# Revit family: Hager-VECTOR-Surface_mounted-IP65-With_Cover-With_DIN-NoHosted-DE-de
name_source: partatom
category: Electrical Equipment
units: mm (PartAtom-declared; Revit-internal decimal feet)

## family parameters
Always vertical = Yes
Cut with Voids When Loaded = No
Maintain Annotation Orientation = No
Panel Configuration = Two Columns, Circuits Across
Part Type = Panelboard
Room Calculation Point = No
Round Connector Dimension = Use Diameter
Shared = No
Work Plane-Based = Yes

## types (87) — shared parameters
Code hager = ADD-EC000214_EU
Default Elevation = 1200 mm
EF000003 - Montageart = Aufputz
EF000007 - Farbe = grau
EF000024 - UV-beständig = No
EF000116 - RAL-Nummer = 7035
EF000118 - Mit Montageplatte = No
EF001062 - EMV-Ausführung = No
EF001134 - DIN-Schiene = Yes
EF004462 - Art der Schließung = sonstige
EF005474 - Schutzart (IP) = IP65
EF006306 - Mit Schloss = No
ETIM class code = EC000214
ETIM class name = Small distribution board
HG000001-Anzahl der Spalten = 1
HG000002-Mit tür = Yes
HG000003-Bereich = VECTOR
HG000005-Dicke = 2 mm  [stored 0.00656168 ft]
HG000006-Flush mounted = No
HG000009-Doppelflügeligen Tür = No
HG000010-Asymmetrische Türen = No
HG000011-Leere Reihen von unten = No
HG000012-Türschwenkwinkel = 90.00°
HG000013-Tür links = No
HG000014-Tür rechts = Yes
HG000015-Sichtbarkeit der Türöffnung = Yes
HG000016-3D-Türsichtbarkeit = Yes
HG000017-Distanz zwischen den Polen = 18 mm  [stored 0.0590551 ft]
HG000060-RAL-number = 7035
HG000099-Onfly Template ID-de-DE = 507532
Manufacturer = Hager
Name BIM&CO = Electricity
Name hager = ADD_Enclosures_EC000214
Reference = Template-Enclosure_EU-EC000214
Uniformat = Low Tension Service & Dist.
Uniformat code = D501001
zero-valued in all types: EF000218 - Einbautiefe, EF000332 - Einbauhöhe, EF000846 - Einbaubreite, EF001131 - Innentiefe, HG000007-Anzahl der leeren Spalten, HG000008-Anzahl der leeren Reihen

## per-type parameters (varying)
| type | BC_METADATA | EF000008 - Breite | EF000040 - Höhe | EF000049 - Tiefe | EF000266 - Anzahl der Reihen | EF001088 - Anbaumöglichkeit | EF002950 - Breite in Teilungseinheiten | EF006244 - Transparenter Deckel/Tür | EF009212 - Ausführung Deckel | EF015776 - Erdungsklemmenblock | EF015777 - Neutralleiterklemmenblock | EF015941 - Signaldurchlassende Tür | HG000004-Herstellerreferenz | HGEF000266-Anzahl der Reihen | HGEF0002950-Breite in Teilungseinheiten |
| VECTOR-Surface_mounted_W310_H552_D151_12_Modular_Spacing-VE312AK | {"ObjectGuid":"03e6f95a-bdcf-4ad5-8e30-8306eb141510","ModelGuid":"49ec60d2-c561-4fc0-8b60-787ba45f202c","VariantGuid":"607cdb30-8050-4ec9-9431-8f6f41ac29e4","Revision":"#11","VariantName":"VECTOR-Surface_mounted_W310_H552_D151_12_Modular_Spacing-VE312AK"} | 310 mm  [stored 1.01706 ft] | 552 mm  [stored 1.81102 ft] | 151 mm  [stored 0.495407 ft] | 3 | Yes | 12 | Yes | geschlossen | Yes | Yes | Yes | VE312AK | 3 | 12 |
| VECTOR-Surface_mounted_W310_H552_D151_36_Modular_Spacing-VE312DK | {"ObjectGuid":"03e6f95a-bdcf-4ad5-8e30-8306eb141510","ModelGuid":"49ec60d2-c561-4fc0-8b60-787ba45f202c","VariantGuid":"d6fdc3a8-bad4-40ab-905a-8434b4d1adf6","Revision":"#11","VariantName":"VECTOR-Surface_mounted_W310_H552_D151_36_Modular_Spacing-VE312DK"} | 310 mm  [stored 1.01706 ft] | 552 mm  [stored 1.81102 ft] | 151 mm  [stored 0.495407 ft] | 3 | Yes | 36 | Yes | geschlossen | No | No | Yes | VE312DK | 3 | 36 |
| VECTOR-Surface_mounted_W310_H552_D151_12_Modular_Spacing-VE312DN | {"ObjectGuid":"03e6f95a-bdcf-4ad5-8e30-8306eb141510","ModelGuid":"49ec60d2-c561-4fc0-8b60-787ba45f202c","VariantGuid":"e0a0b13a-2f78-4e79-9cb4-df8ea80ce2be","Revision":"#11","VariantName":"VECTOR-Surface_mounted_W310_H552_D151_12_Modular_Spacing-VE312DN"} | 310 mm  [stored 1.01706 ft] | 552 mm  [stored 1.81102 ft] | 151 mm  [stored 0.495407 ft] | 3 | Yes | 12 | Yes | geschlossen | Yes | Yes | Yes | VE312DN | 3 | 12 |
| VECTOR-Surface_mounted_W310_H552_D151_12_Modular_Spacing-VE312F | {"ObjectGuid":"03e6f95a-bdcf-4ad5-8e30-8306eb141510","ModelGuid":"49ec60d2-c561-4fc0-8b60-787ba45f202c","VariantGuid":"a51da385-521d-42e7-b15b-fe15b541e67b","Revision":"#11","VariantName":"VECTOR-Surface_mounted_W310_H552_D151_12_Modular_Spacing-VE312F"} | 310 mm  [stored 1.01706 ft] | 552 mm  [stored 1.81102 ft] | 151 mm  [stored 0.495407 ft] | 3 | Yes | 12 | No | geschlossen | Yes | No | Yes | VE312F | 3 | 12 |
| VECTOR-Surface_mounted_W310_H552_D151_12_Modular_Spacing-VE312L | {"ObjectGuid":"03e6f95a-bdcf-4ad5-8e30-8306eb141510","ModelGuid":"49ec60d2-c561-4fc0-8b60-787ba45f202c","VariantGuid":"6e8b8deb-b106-49c2-b92e-4b4428fcabe4","Revision":"#11","VariantName":"VECTOR-Surface_mounted_W310_H552_D151_12_Modular_Spacing-VE312L"} | 310 mm  [stored 1.01706 ft] | 552 mm  [stored 1.81102 ft] | 151 mm  [stored 0.495407 ft] | 3 | Yes | 12 | Yes | mit Ausschnitt | Yes | Yes | Yes | VE312L | 3 | 12 |
| VECTOR-Surface_mounted_W310_H552_D151_36_Modular_Spacing-VE312N | {"ObjectGuid":"03e6f95a-bdcf-4ad5-8e30-8306eb141510","ModelGuid":"49ec60d2-c561-4fc0-8b60-787ba45f202c","VariantGuid":"671be7f2-69a9-4b2d-b5fc-3d919ee885c0","Revision":"#11","VariantName":"VECTOR-Surface_mounted_W310_H552_D151_36_Modular_Spacing-VE312N"} | 310 mm  [stored 1.01706 ft] | 552 mm  [stored 1.81102 ft] | 151 mm  [stored 0.495407 ft] | 3 | Yes | 36 | Yes | geschlossen | Yes | Yes | Yes | VE312N | 3 | 36 |
| VECTOR-Surface_mounted_W310_H552_D151_12_Modular_Spacing-VE312PN | {"ObjectGuid":"03e6f95a-bdcf-4ad5-8e30-8306eb141510","ModelGuid":"49ec60d2-c561-4fc0-8b60-787ba45f202c","VariantGuid":"5d3d3522-fa09-46ff-862d-f1016403435b","Revision":"#11","VariantName":"VECTOR-Surface_mounted_W310_H552_D151_12_Modular_Spacing-VE312PN"} | 310 mm  [stored 1.01706 ft] | 552 mm  [stored 1.81102 ft] | 151 mm  [stored 0.495407 ft] | 3 | Yes | 12 | Yes | geschlossen | No | No | Yes | VE312PN | 3 | 12 |
| VECTOR-Surface_mounted_W310_H552_D151_12_Modular_Spacing-VE312S | {"ObjectGuid":"03e6f95a-bdcf-4ad5-8e30-8306eb141510","ModelGuid":"49ec60d2-c561-4fc0-8b60-787ba45f202c","VariantGuid":"071b8a18-1f4b-4499-85d7-62c8f9297f1b","Revision":"#11","VariantName":"VECTOR-Surface_mounted_W310_H552_D151_12_Modular_Spacing-VE312S"} | 310 mm  [stored 1.01706 ft] | 552 mm  [stored 1.81102 ft] | 151 mm  [stored 0.495407 ft] | 3 | Yes | 12 | No | geschlossen | Yes | Yes | Yes | VE312S | 3 | 12 |
| VECTOR-Surface_mounted_W310_H552_D151_12_Modular_Spacing-VE312SN | {"ObjectGuid":"03e6f95a-bdcf-4ad5-8e30-8306eb141510","ModelGuid":"49ec60d2-c561-4fc0-8b60-787ba45f202c","VariantGuid":"53cd1ff2-2b29-469f-bbba-6836d89362b1","Revision":"#11","VariantName":"VECTOR-Surface_mounted_W310_H552_D151_12_Modular_Spacing-VE312SN"} | 310 mm  [stored 1.01706 ft] | 552 mm  [stored 1.81102 ft] | 151 mm  [stored 0.495407 ft] | 3 | Yes | 12 | Yes | mit Ausschnitt | No | No | Yes | VE312SN | 3 | 12 |
| VECTOR-Surface_mounted_W418_H602_D151_18_Modular_Spacing-VE318AK | {"ObjectGuid":"03e6f95a-bdcf-4ad5-8e30-8306eb141510","ModelGuid":"49ec60d2-c561-4fc0-8b60-787ba45f202c","VariantGuid":"4236e502-4e81-4f1a-bf8d-444f96f3dce0","Revision":"#11","VariantName":"VECTOR-Surface_mounted_W418_H602_D151_18_Modular_Spacing-VE318AK"} | 418 mm  [stored 1.37139 ft] | 602 mm  [stored 1.97507 ft] | 151 mm  [stored 0.495407 ft] | 3 | Yes | 18 | Yes | geschlossen | Yes | Yes | Yes | VE318AK | 3 | 18 |
| VECTOR-Surface_mounted_W418_H602_D151_54_Modular_Spacing-VE318DK | {"ObjectGuid":"03e6f95a-bdcf-4ad5-8e30-8306eb141510","ModelGuid":"49ec60d2-c561-4fc0-8b60-787ba45f202c","VariantGuid":"c878d14d-feb4-4f4e-b568-957a8d41c48b","Revision":"#11","VariantName":"VECTOR-Surface_mounted_W418_H602_D151_54_Modular_Spacing-VE318DK"} | 418 mm  [stored 1.37139 ft] | 602 mm  [stored 1.97507 ft] | 151 mm  [stored 0.495407 ft] | 3 | Yes | 54 | Yes | geschlossen | No | No | Yes | VE318DK | 3 | 54 |
| VECTOR-Surface_mounted_W418_H602_D151_18_Modular_Spacing-VE318DN | {"ObjectGuid":"03e6f95a-bdcf-4ad5-8e30-8306eb141510","ModelGuid":"49ec60d2-c561-4fc0-8b60-787ba45f202c","VariantGuid":"d9c7745d-cdbe-4532-855f-0ffb42954d71","Revision":"#11","VariantName":"VECTOR-Surface_mounted_W418_H602_D151_18_Modular_Spacing-VE318DN"} | 418 mm  [stored 1.37139 ft] | 602 mm  [stored 1.97507 ft] | 151 mm  [stored 0.495407 ft] | 3 | Yes | 18 | Yes | geschlossen | Yes | Yes | Yes | VE318DN | 3 | 18 |
| VECTOR-Surface_mounted_W111_H175_D93_3_Modular_Spacing-VE103A | {"ObjectGuid":"03e6f95a-bdcf-4ad5-8e30-8306eb141510","ModelGuid":"49ec60d2-c561-4fc0-8b60-787ba45f202c","VariantGuid":"03d529d2-2e61-454c-967e-f33b8fa2df03","Revision":"#11","VariantName":"VECTOR-Surface_mounted_W111_H175_D93_3_Modular_Spacing-VE103A"} | 111 mm | 175 mm  [stored 0.574147 ft] | 93 mm  [stored 0.305118 ft] | 1 | Yes | 3 | Yes | geschlossen | Yes | No | Yes | VE103A | 1 | 3 |
| VECTOR-Surface_mounted_W110_H175_D93_3_Modular_Spacing-VE103D | {"ObjectGuid":"03e6f95a-bdcf-4ad5-8e30-8306eb141510","ModelGuid":"49ec60d2-c561-4fc0-8b60-787ba45f202c","VariantGuid":"fc0e37b7-f710-4ef9-b472-aa3ce9bbbe3a","Revision":"#11","VariantName":"VECTOR-Surface_mounted_W110_H175_D93_3_Modular_Spacing-VE103D"} | 110 mm  [stored 0.360892 ft] | 175 mm  [stored 0.574147 ft] | 93 mm  [stored 0.305118 ft] | 1 | Yes | 3 | Yes | geschlossen | Yes | No | Yes | VE103D | 1 | 3 |
| VECTOR-Surface_mounted_W111_H175_D93_3_Modular_Spacing-VE103F | {"ObjectGuid":"03e6f95a-bdcf-4ad5-8e30-8306eb141510","ModelGuid":"49ec60d2-c561-4fc0-8b60-787ba45f202c","VariantGuid":"b8136d2f-5e20-4b9a-a4f7-e4fc681256c1","Revision":"#11","VariantName":"VECTOR-Surface_mounted_W111_H175_D93_3_Modular_Spacing-VE103F"} | 111 mm | 175 mm  [stored 0.574147 ft] | 93 mm  [stored 0.305118 ft] | 1 | No | 3 | No | geschlossen | No | No | No | VE103F | 1 | 3 |
| VECTOR-Surface_mounted_W111_H175_D93_0_Modular_Spacing-VE103L | {"ObjectGuid":"03e6f95a-bdcf-4ad5-8e30-8306eb141510","ModelGuid":"49ec60d2-c561-4fc0-8b60-787ba45f202c","VariantGuid":"d248ef2d-5bbd-4438-8b05-bad34478cf64","Revision":"#11","VariantName":"VECTOR-Surface_mounted_W111_H175_D93_0_Modular_Spacing-VE103L"} | 111 mm | 175 mm  [stored 0.574147 ft] | 93 mm  [stored 0.305118 ft] | 1 | No | 0 | No | geschlossen | No | No | No | VE103L | 1 | 0 |
| VECTOR-Surface_mounted_W111_H175_D93_3_Modular_Spacing-VE103N | {"ObjectGuid":"03e6f95a-bdcf-4ad5-8e30-8306eb141510","ModelGuid":"49ec60d2-c561-4fc0-8b60-787ba45f202c","VariantGuid":"ecea2f8b-0722-4d77-ba9b-281cfc718821","Revision":"#11","VariantName":"VECTOR-Surface_mounted_W111_H175_D93_3_Modular_Spacing-VE103N"} | 111 mm | 175 mm  [stored 0.574147 ft] | 93 mm  [stored 0.305118 ft] | 1 | Yes | 3 | Yes | geschlossen | Yes | Yes | Yes | VE103N | 1 | 3 |
| VECTOR-Surface_mounted_W111_H175_D93_3_Modular_Spacing-VE103PN | {"ObjectGuid":"03e6f95a-bdcf-4ad5-8e30-8306eb141510","ModelGuid":"49ec60d2-c561-4fc0-8b60-787ba45f202c","VariantGuid":"70e002fb-47ab-4400-88c9-3d78650046f9","Revision":"#11","VariantName":"VECTOR-Surface_mounted_W111_H175_D93_3_Modular_Spacing-VE103PN"} | 111 mm | 175 mm  [stored 0.574147 ft] | 93 mm  [stored 0.305118 ft] | 1 | Yes | 3 | Yes | mit Ausschnitt | No | No | Yes | VE103PN | 1 | 3 |
| VECTOR-Surface_mounted_W111_H175_D93_3_Modular_Spacing-VE103S | {"ObjectGuid":"03e6f95a-bdcf-4ad5-8e30-8306eb141510","ModelGuid":"49ec60d2-c561-4fc0-8b60-787ba45f202c","VariantGuid":"b04d4e39-4e2e-4946-91a1-f15623b818ea","Revision":"#11","VariantName":"VECTOR-Surface_mounted_W111_H175_D93_3_Modular_Spacing-VE103S"} | 111 mm | 175 mm  [stored 0.574147 ft] | 93 mm  [stored 0.305118 ft] | 1 | Yes | 3 | Yes | geschlossen | Yes | Yes | Yes | VE103S | 1 | 3 |
| VECTOR-Surface_mounted_W111_H175_D93_3_Modular_Spacing-VE103SN | {"ObjectGuid":"03e6f95a-bdcf-4ad5-8e30-8306eb141510","ModelGuid":"49ec60d2-c561-4fc0-8b60-787ba45f202c","VariantGuid":"80d78b52-09ce-482e-8377-596ddb527fc9","Revision":"#11","VariantName":"VECTOR-Surface_mounted_W111_H175_D93_3_Modular_Spacing-VE103SN"} | 111 mm | 175 mm  [stored 0.574147 ft] | 93 mm  [stored 0.305118 ft] | 1 | Yes | 3 | Yes | mit Ausschnitt | No | No | Yes | VE103SN | 1 | 3 |
| VECTOR-Surface_mounted_W165_H190_D113_6_Modular_Spacing-VE106A | {"ObjectGuid":"03e6f95a-bdcf-4ad5-8e30-8306eb141510","ModelGuid":"49ec60d2-c561-4fc0-8b60-787ba45f202c","VariantGuid":"59e713e8-78d4-49eb-9629-265d8f4a412e","Revision":"#11","VariantName":"VECTOR-Surface_mounted_W165_H190_D113_6_Modular_Spacing-VE106A"} | 165 mm | 190 mm  [stored 0.62336 ft] | 113 mm  [stored 0.370735 ft] | 1 | Yes | 6 | Yes | geschlossen | Yes | No | Yes | VE106A | 1 | 6 |
| VECTOR-Surface_mounted_W164_H190_D113_6_Modular_Spacing-VE106D | {"ObjectGuid":"03e6f95a-bdcf-4ad5-8e30-8306eb141510","ModelGuid":"49ec60d2-c561-4fc0-8b60-787ba45f202c","VariantGuid":"387c52ea-65d6-420b-96e2-5242636dd8b7","Revision":"#11","VariantName":"VECTOR-Surface_mounted_W164_H190_D113_6_Modular_Spacing-VE106D"} | 164 mm  [stored 0.538058 ft] | 190 mm  [stored 0.62336 ft] | 113 mm  [stored 0.370735 ft] | 1 | Yes | 6 | Yes | geschlossen | Yes | No | Yes | VE106D | 1 | 6 |
| VECTOR-Surface_mounted_W165_H190_D113_6_Modular_Spacing-VE106F | {"ObjectGuid":"03e6f95a-bdcf-4ad5-8e30-8306eb141510","ModelGuid":"49ec60d2-c561-4fc0-8b60-787ba45f202c","VariantGuid":"caaf4306-a693-4fdd-bfaf-0454a5d81484","Revision":"#11","VariantName":"VECTOR-Surface_mounted_W165_H190_D113_6_Modular_Spacing-VE106F"} | 165 mm | 190 mm  [stored 0.62336 ft] | 113 mm  [stored 0.370735 ft] | 1 | Yes | 6 | No | geschlossen | Yes | No | Yes | VE106F | 1 | 6 |
| VECTOR-Surface_mounted_W165_H190_D113_0_Modular_Spacing-VE106L | {"ObjectGuid":"03e6f95a-bdcf-4ad5-8e30-8306eb141510","ModelGuid":"49ec60d2-c561-4fc0-8b60-787ba45f202c","VariantGuid":"a5921312-03c2-41db-88c9-9f37a279dd1f","Revision":"#11","VariantName":"VECTOR-Surface_mounted_W165_H190_D113_0_Modular_Spacing-VE106L"} | 165 mm | 190 mm  [stored 0.62336 ft] | 113 mm  [stored 0.370735 ft] | 1 | No | 0 | No | geschlossen | No | No | No | VE106L | 1 | 0 |
| VECTOR-Surface_mounted_W165_H190_D113_6_Modular_Spacing-VE106N | {"ObjectGuid":"03e6f95a-bdcf-4ad5-8e30-8306eb141510","ModelGuid":"49ec60d2-c561-4fc0-8b60-787ba45f202c","VariantGuid":"53309e99-1cf9-4b5d-b833-e050c4f3a3a2","Revision":"#11","VariantName":"VECTOR-Surface_mounted_W165_H190_D113_6_Modular_Spacing-VE106N"} | 165 mm | 190 mm  [stored 0.62336 ft] | 113 mm  [stored 0.370735 ft] | 1 | Yes | 6 | Yes | geschlossen | Yes | Yes | Yes | VE106N | 1 | 6 |
| VECTOR-Surface_mounted_W165_H190_D113_6_Modular_Spacing-VE106PN | {"ObjectGuid":"03e6f95a-bdcf-4ad5-8e30-8306eb141510","ModelGuid":"49ec60d2-c561-4fc0-8b60-787ba45f202c","VariantGuid":"698bf969-04a1-4a44-b5de-9a0be0d43178","Revision":"#11","VariantName":"VECTOR-Surface_mounted_W165_H190_D113_6_Modular_Spacing-VE106PN"} | 165 mm | 190 mm  [stored 0.62336 ft] | 113 mm  [stored 0.370735 ft] | 1 | Yes | 6 | Yes | geschlossen | No | No | Yes | VE106PN | 1 | 6 |
| VECTOR-Surface_mounted_W165_H190_D113_6_Modular_Spacing-VE106S | {"ObjectGuid":"03e6f95a-bdcf-4ad5-8e30-8306eb141510","ModelGuid":"49ec60d2-c561-4fc0-8b60-787ba45f202c","VariantGuid":"96432657-48a8-4170-9d04-70eb89fd6238","Revision":"#11","VariantName":"VECTOR-Surface_mounted_W165_H190_D113_6_Modular_Spacing-VE106S"} | 165 mm | 190 mm  [stored 0.62336 ft] | 113 mm  [stored 0.370735 ft] | 1 | Yes | 6 | Yes | geschlossen | Yes | Yes | Yes | VE106S | 1 | 6 |
| VECTOR-Surface_mounted_W165_H190_D113_6_Modular_Spacing-VE106SN | {"ObjectGuid":"03e6f95a-bdcf-4ad5-8e30-8306eb141510","ModelGuid":"49ec60d2-c561-4fc0-8b60-787ba45f202c","VariantGuid":"1a015454-a905-4075-9f93-b73a44b6c4df","Revision":"#11","VariantName":"VECTOR-Surface_mounted_W165_H190_D113_6_Modular_Spacing-VE106SN"} | 165 mm | 190 mm  [stored 0.62336 ft] | 113 mm  [stored 0.370735 ft] | 1 | Yes | 6 | Yes | mit Ausschnitt | No | No | Yes | VE106SN | 1 | 6 |
| VECTOR-Surface_mounted_W237_H210_D114_10_Modular_Spacing-VE110A | {"ObjectGuid":"03e6f95a-bdcf-4ad5-8e30-8306eb141510","ModelGuid":"49ec60d2-c561-4fc0-8b60-787ba45f202c","VariantGuid":"b11a67ab-c6d2-44bd-912e-a112c9473f36","Revision":"#11","VariantName":"VECTOR-Surface_mounted_W237_H210_D114_10_Modular_Spacing-VE110A"} | 237 mm  [stored 0.777559 ft] | 210 mm  [stored 0.688976 ft] | 114 mm  [stored 0.374016 ft] | 1 | Yes | 10 | Yes | geschlossen | Yes | No | Yes | VE110A | 1 | 10 |
| VECTOR-Surface_mounted_W236_H210_D114_10_Modular_Spacing-VE110D | {"ObjectGuid":"03e6f95a-bdcf-4ad5-8e30-8306eb141510","ModelGuid":"49ec60d2-c561-4fc0-8b60-787ba45f202c","VariantGuid":"f7057bc0-4218-4225-9d6e-bddab06c837f","Revision":"#11","VariantName":"VECTOR-Surface_mounted_W236_H210_D114_10_Modular_Spacing-VE110D"} | 236 mm | 210 mm  [stored 0.688976 ft] | 114 mm  [stored 0.374016 ft] | 1 | Yes | 10 | Yes | geschlossen | Yes | No | Yes | VE110D | 1 | 10 |
| VECTOR-Surface_mounted_W237_H210_D114_10_Modular_Spacing-VE110F | {"ObjectGuid":"03e6f95a-bdcf-4ad5-8e30-8306eb141510","ModelGuid":"49ec60d2-c561-4fc0-8b60-787ba45f202c","VariantGuid":"8bf2bf94-76b4-4685-8aaa-f9cad71004cb","Revision":"#11","VariantName":"VECTOR-Surface_mounted_W237_H210_D114_10_Modular_Spacing-VE110F"} | 237 mm  [stored 0.777559 ft] | 210 mm  [stored 0.688976 ft] | 114 mm  [stored 0.374016 ft] | 1 | Yes | 10 | No | geschlossen | Yes | No | Yes | VE110F | 1 | 10 |
| VECTOR-Surface_mounted_W237_H210_D114_10_Modular_Spacing-VE110L | {"ObjectGuid":"03e6f95a-bdcf-4ad5-8e30-8306eb141510","ModelGuid":"49ec60d2-c561-4fc0-8b60-787ba45f202c","VariantGuid":"6016af11-71cd-403b-afe5-f7489500a834","Revision":"#11","VariantName":"VECTOR-Surface_mounted_W237_H210_D114_10_Modular_Spacing-VE110L"} | 237 mm  [stored 0.777559 ft] | 210 mm  [stored 0.688976 ft] | 114 mm  [stored 0.374016 ft] | 1 | Yes | 10 | Yes | mit Ausschnitt | Yes | Yes | Yes | VE110L | 1 | 10 |
| VECTOR-Surface_mounted_W237_H210_D114_10_Modular_Spacing-VE110N | {"ObjectGuid":"03e6f95a-bdcf-4ad5-8e30-8306eb141510","ModelGuid":"49ec60d2-c561-4fc0-8b60-787ba45f202c","VariantGuid":"696b45c9-7071-4951-93bb-d903358c74f0","Revision":"#11","VariantName":"VECTOR-Surface_mounted_W237_H210_D114_10_Modular_Spacing-VE110N"} | 237 mm  [stored 0.777559 ft] | 210 mm  [stored 0.688976 ft] | 114 mm  [stored 0.374016 ft] | 1 | Yes | 10 | Yes | geschlossen | Yes | Yes | Yes | VE110N | 1 | 10 |
| VECTOR-Surface_mounted_W237_H210_D114_10_Modular_Spacing-VE110PN | {"ObjectGuid":"03e6f95a-bdcf-4ad5-8e30-8306eb141510","ModelGuid":"49ec60d2-c561-4fc0-8b60-787ba45f202c","VariantGuid":"6eb31640-a545-495b-b743-93b4930531f3","Revision":"#11","VariantName":"VECTOR-Surface_mounted_W237_H210_D114_10_Modular_Spacing-VE110PN"} | 237 mm  [stored 0.777559 ft] | 210 mm  [stored 0.688976 ft] | 114 mm  [stored 0.374016 ft] | 1 | Yes | 10 | Yes | geschlossen | No | No | Yes | VE110PN | 1 | 10 |
| VECTOR-Surface_mounted_W237_H210_D114_10_Modular_Spacing-VE110S | {"ObjectGuid":"03e6f95a-bdcf-4ad5-8e30-8306eb141510","ModelGuid":"49ec60d2-c561-4fc0-8b60-787ba45f202c","VariantGuid":"718ed4c0-d5d9-43e5-8292-5012003df886","Revision":"#11","VariantName":"VECTOR-Surface_mounted_W237_H210_D114_10_Modular_Spacing-VE110S"} | 237 mm  [stored 0.777559 ft] | 210 mm  [stored 0.688976 ft] | 114 mm  [stored 0.374016 ft] | 1 | Yes | 10 | Yes | geschlossen | Yes | Yes | Yes | VE110S | 1 | 10 |
| VECTOR-Surface_mounted_W237_H210_D114_10_Modular_Spacing-VE110SN | {"ObjectGuid":"03e6f95a-bdcf-4ad5-8e30-8306eb141510","ModelGuid":"49ec60d2-c561-4fc0-8b60-787ba45f202c","VariantGuid":"16e74280-12af-4dda-90d3-823f23ba35df","Revision":"#11","VariantName":"VECTOR-Surface_mounted_W237_H210_D114_10_Modular_Spacing-VE110SN"} | 237 mm  [stored 0.777559 ft] | 210 mm  [stored 0.688976 ft] | 114 mm  [stored 0.374016 ft] | 1 | Yes | 10 | Yes | geschlossen | No | No | Yes | VE110SN | 1 | 10 |
| VECTOR-Surface_mounted_W310_H302_D151_12_Modular_Spacing-VE112AK | {"ObjectGuid":"03e6f95a-bdcf-4ad5-8e30-8306eb141510","ModelGuid":"49ec60d2-c561-4fc0-8b60-787ba45f202c","VariantGuid":"b2027f19-49bb-4b3f-80ab-c96eafe2390f","Revision":"#11","VariantName":"VECTOR-Surface_mounted_W310_H302_D151_12_Modular_Spacing-VE112AK"} | 310 mm  [stored 1.01706 ft] | 302 mm  [stored 0.990814 ft] | 151 mm  [stored 0.495407 ft] | 1 | Yes | 12 | Yes | geschlossen | Yes | Yes | Yes | VE112AK | 1 | 12 |
| VECTOR-Surface_mounted_W310_H302_D151_12_Modular_Spacing-VE112DK | {"ObjectGuid":"03e6f95a-bdcf-4ad5-8e30-8306eb141510","ModelGuid":"49ec60d2-c561-4fc0-8b60-787ba45f202c","VariantGuid":"18436d3b-76e5-4c5e-b002-14b8bb07869d","Revision":"#11","VariantName":"VECTOR-Surface_mounted_W310_H302_D151_12_Modular_Spacing-VE112DK"} | 310 mm  [stored 1.01706 ft] | 302 mm  [stored 0.990814 ft] | 151 mm  [stored 0.495407 ft] | 1 | Yes | 12 | Yes | geschlossen | No | No | Yes | VE112DK | 1 | 12 |
| VECTOR-Surface_mounted_W310_H302_D151_12_Modular_Spacing-VE112DN | {"ObjectGuid":"03e6f95a-bdcf-4ad5-8e30-8306eb141510","ModelGuid":"49ec60d2-c561-4fc0-8b60-787ba45f202c","VariantGuid":"9eaee06a-e50b-4124-a356-35a9b004a430","Revision":"#11","VariantName":"VECTOR-Surface_mounted_W310_H302_D151_12_Modular_Spacing-VE112DN"} | 310 mm  [stored 1.01706 ft] | 302 mm  [stored 0.990814 ft] | 151 mm  [stored 0.495407 ft] | 1 | Yes | 12 | Yes | geschlossen | Yes | Yes | Yes | VE112DN | 1 | 12 |
| VECTOR-Surface_mounted_W310_H302_D151_12_Modular_Spacing-VE112F | {"ObjectGuid":"03e6f95a-bdcf-4ad5-8e30-8306eb141510","ModelGuid":"49ec60d2-c561-4fc0-8b60-787ba45f202c","VariantGuid":"7d39984b-ddb7-4a7a-93c1-b2c1b5821d33","Revision":"#11","VariantName":"VECTOR-Surface_mounted_W310_H302_D151_12_Modular_Spacing-VE112F"} | 310 mm  [stored 1.01706 ft] | 302 mm  [stored 0.990814 ft] | 151 mm  [stored 0.495407 ft] | 1 | Yes | 12 | No | geschlossen | Yes | No | Yes | VE112F | 1 | 12 |
| VECTOR-Surface_mounted_W310_H302_D151_12_Modular_Spacing-VE112L | {"ObjectGuid":"03e6f95a-bdcf-4ad5-8e30-8306eb141510","ModelGuid":"49ec60d2-c561-4fc0-8b60-787ba45f202c","VariantGuid":"4e778da1-5b57-4577-8130-41b5377e5de9","Revision":"#11","VariantName":"VECTOR-Surface_mounted_W310_H302_D151_12_Modular_Spacing-VE112L"} | 310 mm  [stored 1.01706 ft] | 302 mm  [stored 0.990814 ft] | 151 mm  [stored 0.495407 ft] | 1 | Yes | 12 | Yes | mit Ausschnitt | Yes | Yes | Yes | VE112L | 1 | 12 |
| VECTOR-Surface_mounted_W310_H302_D151_12_Modular_Spacing-VE112N | {"ObjectGuid":"03e6f95a-bdcf-4ad5-8e30-8306eb141510","ModelGuid":"49ec60d2-c561-4fc0-8b60-787ba45f202c","VariantGuid":"fb0d047a-9a66-40fb-b157-bd6c53aa5997","Revision":"#11","VariantName":"VECTOR-Surface_mounted_W310_H302_D151_12_Modular_Spacing-VE112N"} | 310 mm  [stored 1.01706 ft] | 302 mm  [stored 0.990814 ft] | 151 mm  [stored 0.495407 ft] | 1 | Yes | 12 | Yes | geschlossen | Yes | Yes | Yes | VE112N | 1 | 12 |
| VECTOR-Surface_mounted_W310_H302_D151_12_Modular_Spacing-VE112PN | {"ObjectGuid":"03e6f95a-bdcf-4ad5-8e30-8306eb141510","ModelGuid":"49ec60d2-c561-4fc0-8b60-787ba45f202c","VariantGuid":"a2870ead-c474-4726-b496-7a5ea67d2325","Revision":"#11","VariantName":"VECTOR-Surface_mounted_W310_H302_D151_12_Modular_Spacing-VE112PN"} | 310 mm  [stored 1.01706 ft] | 302 mm  [stored 0.990814 ft] | 151 mm  [stored 0.495407 ft] | 1 | Yes | 12 | Yes | geschlossen | No | No | Yes | VE112PN | 1 | 12 |
| VECTOR-Surface_mounted_W310_H302_D151_12_Modular_Spacing-VE112S | {"ObjectGuid":"03e6f95a-bdcf-4ad5-8e30-8306eb141510","ModelGuid":"49ec60d2-c561-4fc0-8b60-787ba45f202c","VariantGuid":"3c8079dd-79bc-47aa-8600-133633fd323e","Revision":"#11","VariantName":"VECTOR-Surface_mounted_W310_H302_D151_12_Modular_Spacing-VE112S"} | 310 mm  [stored 1.01706 ft] | 302 mm  [stored 0.990814 ft] | 151 mm  [stored 0.495407 ft] | 1 | Yes | 12 | No | geschlossen | Yes | Yes | Yes | VE112S | 1 | 12 |
| VECTOR-Surface_mounted_W310_H302_D151_12_Modular_Spacing-VE112SN | {"ObjectGuid":"03e6f95a-bdcf-4ad5-8e30-8306eb141510","ModelGuid":"49ec60d2-c561-4fc0-8b60-787ba45f202c","VariantGuid":"3c7b340f-69d5-4c4d-9cd8-371d4f75cba0","Revision":"#11","VariantName":"VECTOR-Surface_mounted_W310_H302_D151_12_Modular_Spacing-VE112SN"} | 310 mm  [stored 1.01706 ft] | 302 mm  [stored 0.990814 ft] | 151 mm  [stored 0.495407 ft] | 1 | Yes | 12 | Yes | geschlossen | No | No | Yes | VE112SN | 1 | 12 |
| VECTOR-Surface_mounted_W418_H302_D151_18_Modular_Spacing-VE118AK | {"ObjectGuid":"03e6f95a-bdcf-4ad5-8e30-8306eb141510","ModelGuid":"49ec60d2-c561-4fc0-8b60-787ba45f202c","VariantGuid":"54c855c4-48d5-47df-9d35-d1d1dbd41270","Revision":"#11","VariantName":"VECTOR-Surface_mounted_W418_H302_D151_18_Modular_Spacing-VE118AK"} | 418 mm  [stored 1.37139 ft] | 302 mm  [stored 0.990814 ft] | 151 mm  [stored 0.495407 ft] | 1 | Yes | 18 | Yes | geschlossen | Yes | Yes | Yes | VE118AK | 1 | 18 |
| VECTOR-Surface_mounted_W418_H302_D151_18_Modular_Spacing-VE118DK | {"ObjectGuid":"03e6f95a-bdcf-4ad5-8e30-8306eb141510","ModelGuid":"49ec60d2-c561-4fc0-8b60-787ba45f202c","VariantGuid":"306ed917-eff4-436b-84e0-fbb57f547a12","Revision":"#11","VariantName":"VECTOR-Surface_mounted_W418_H302_D151_18_Modular_Spacing-VE118DK"} | 418 mm  [stored 1.37139 ft] | 302 mm  [stored 0.990814 ft] | 151 mm  [stored 0.495407 ft] | 1 | Yes | 18 | Yes | geschlossen | No | No | Yes | VE118DK | 1 | 18 |
| VECTOR-Surface_mounted_W418_H302_D151_18_Modular_Spacing-VE118DN | {"ObjectGuid":"03e6f95a-bdcf-4ad5-8e30-8306eb141510","ModelGuid":"49ec60d2-c561-4fc0-8b60-787ba45f202c","VariantGuid":"ef4b0461-6a43-4c77-923f-28a44a0d5b48","Revision":"#11","VariantName":"VECTOR-Surface_mounted_W418_H302_D151_18_Modular_Spacing-VE118DN"} | 418 mm  [stored 1.37139 ft] | 302 mm  [stored 0.990814 ft] | 151 mm  [stored 0.495407 ft] | 1 | Yes | 18 | Yes | geschlossen | Yes | Yes | Yes | VE118DN | 1 | 18 |
| VECTOR-Surface_mounted_W418_H302_D151_18_Modular_Spacing-VE118F | {"ObjectGuid":"03e6f95a-bdcf-4ad5-8e30-8306eb141510","ModelGuid":"49ec60d2-c561-4fc0-8b60-787ba45f202c","VariantGuid":"5ad9fa9d-35bc-40e0-9408-0918bffe310d","Revision":"#11","VariantName":"VECTOR-Surface_mounted_W418_H302_D151_18_Modular_Spacing-VE118F"} | 418 mm  [stored 1.37139 ft] | 302 mm  [stored 0.990814 ft] | 151 mm  [stored 0.495407 ft] | 1 | No | 18 | No | geschlossen | No | No | No | VE118F | 1 | 18 |
| VECTOR-Surface_mounted_W418_H302_D151_18_Modular_Spacing-VE118L | {"ObjectGuid":"03e6f95a-bdcf-4ad5-8e30-8306eb141510","ModelGuid":"49ec60d2-c561-4fc0-8b60-787ba45f202c","VariantGuid":"15335ba9-7b2a-4522-84fc-24a403a62078","Revision":"#11","VariantName":"VECTOR-Surface_mounted_W418_H302_D151_18_Modular_Spacing-VE118L"} | 418 mm  [stored 1.37139 ft] | 302 mm  [stored 0.990814 ft] | 151 mm  [stored 0.495407 ft] | 1 | Yes | 18 | Yes | mit Ausschnitt | Yes | Yes | Yes | VE118L | 1 | 18 |
| VECTOR-Surface_mounted_W418_H302_D151_18_Modular_Spacing-VE118N | {"ObjectGuid":"03e6f95a-bdcf-4ad5-8e30-8306eb141510","ModelGuid":"49ec60d2-c561-4fc0-8b60-787ba45f202c","VariantGuid":"1327d3c5-9e58-4b28-9b79-69a5fb447bac","Revision":"#11","VariantName":"VECTOR-Surface_mounted_W418_H302_D151_18_Modular_Spacing-VE118N"} | 418 mm  [stored 1.37139 ft] | 302 mm  [stored 0.990814 ft] | 151 mm  [stored 0.495407 ft] | 1 | Yes | 18 | Yes | geschlossen | No | No | Yes | VE118N | 1 | 18 |
| VECTOR-Surface_mounted_W418_H302_D151_18_Modular_Spacing-VE118PN | {"ObjectGuid":"03e6f95a-bdcf-4ad5-8e30-8306eb141510","ModelGuid":"49ec60d2-c561-4fc0-8b60-787ba45f202c","VariantGuid":"e1e8b8cc-9500-4b59-bad5-fb61cfe21810","Revision":"#11","VariantName":"VECTOR-Surface_mounted_W418_H302_D151_18_Modular_Spacing-VE118PN"} | 418 mm  [stored 1.37139 ft] | 302 mm  [stored 0.990814 ft] | 151 mm  [stored 0.495407 ft] | 1 | Yes | 18 | Yes | geschlossen | No | No | Yes | VE118PN | 1 | 18 |
| VECTOR-Surface_mounted_W418_H302_D151_18_Modular_Spacing-VE118S | {"ObjectGuid":"03e6f95a-bdcf-4ad5-8e30-8306eb141510","ModelGuid":"49ec60d2-c561-4fc0-8b60-787ba45f202c","VariantGuid":"ff1ca60e-1604-4ae3-bc03-0a6eb021a908","Revision":"#11","VariantName":"VECTOR-Surface_mounted_W418_H302_D151_18_Modular_Spacing-VE118S"} | 418 mm  [stored 1.37139 ft] | 302 mm  [stored 0.990814 ft] | 151 mm  [stored 0.495407 ft] | 1 | Yes | 18 | No | geschlossen | Yes | Yes | Yes | VE118S | 1 | 18 |
| VECTOR-Surface_mounted_W418_H302_D151_18_Modular_Spacing-VE118SN | {"ObjectGuid":"03e6f95a-bdcf-4ad5-8e30-8306eb141510","ModelGuid":"49ec60d2-c561-4fc0-8b60-787ba45f202c","VariantGuid":"c504e401-cd70-418b-9396-b99c4b6bdd2d","Revision":"#11","VariantName":"VECTOR-Surface_mounted_W418_H302_D151_18_Modular_Spacing-VE118SN"} | 418 mm  [stored 1.37139 ft] | 302 mm  [stored 0.990814 ft] | 151 mm  [stored 0.495407 ft] | 1 | Yes | 18 | Yes | geschlossen | No | No | Yes | VE118SN | 1 | 18 |
| VECTOR-Surface_mounted_W310_H427_D151_12_Modular_Spacing-VE212AK | {"ObjectGuid":"03e6f95a-bdcf-4ad5-8e30-8306eb141510","ModelGuid":"49ec60d2-c561-4fc0-8b60-787ba45f202c","VariantGuid":"820e874e-4dd4-43db-9fe5-41251723e695","Revision":"#11","VariantName":"VECTOR-Surface_mounted_W310_H427_D151_12_Modular_Spacing-VE212AK"} | 310 mm  [stored 1.01706 ft] | 427 mm  [stored 1.40092 ft] | 151 mm  [stored 0.495407 ft] | 2 | Yes | 12 | Yes | geschlossen | Yes | Yes | Yes | VE212AK | 2 | 12 |
| VECTOR-Surface_mounted_W310_H427_D151_24_Modular_Spacing-VE212DK | {"ObjectGuid":"03e6f95a-bdcf-4ad5-8e30-8306eb141510","ModelGuid":"49ec60d2-c561-4fc0-8b60-787ba45f202c","VariantGuid":"950d921f-a8d4-469b-83c1-07335ce2f737","Revision":"#11","VariantName":"VECTOR-Surface_mounted_W310_H427_D151_24_Modular_Spacing-VE212DK"} | 310 mm  [stored 1.01706 ft] | 427 mm  [stored 1.40092 ft] | 151 mm  [stored 0.495407 ft] | 2 | Yes | 24 | Yes | geschlossen | No | No | Yes | VE212DK | 2 | 24 |
| VECTOR-Surface_mounted_W310_H427_D151_12_Modular_Spacing-VE212DN | {"ObjectGuid":"03e6f95a-bdcf-4ad5-8e30-8306eb141510","ModelGuid":"49ec60d2-c561-4fc0-8b60-787ba45f202c","VariantGuid":"d7d97ec8-ae20-4a18-b166-f9d71ec0b08f","Revision":"#11","VariantName":"VECTOR-Surface_mounted_W310_H427_D151_12_Modular_Spacing-VE212DN"} | 310 mm  [stored 1.01706 ft] | 427 mm  [stored 1.40092 ft] | 151 mm  [stored 0.495407 ft] | 2 | Yes | 12 | Yes | geschlossen | Yes | Yes | Yes | VE212DN | 2 | 12 |
| VECTOR-Surface_mounted_W310_H427_D151_12_Modular_Spacing-VE212F | {"ObjectGuid":"03e6f95a-bdcf-4ad5-8e30-8306eb141510","ModelGuid":"49ec60d2-c561-4fc0-8b60-787ba45f202c","VariantGuid":"06a3a886-9f94-42bf-94d8-467addb789c4","Revision":"#11","VariantName":"VECTOR-Surface_mounted_W310_H427_D151_12_Modular_Spacing-VE212F"} | 310 mm  [stored 1.01706 ft] | 427 mm  [stored 1.40092 ft] | 151 mm  [stored 0.495407 ft] | 2 | Yes | 12 | No | geschlossen | Yes | No | Yes | VE212F | 2 | 12 |
| VECTOR-Surface_mounted_W310_H427_D151_12_Modular_Spacing-VE212L | {"ObjectGuid":"03e6f95a-bdcf-4ad5-8e30-8306eb141510","ModelGuid":"49ec60d2-c561-4fc0-8b60-787ba45f202c","VariantGuid":"a1f1a181-b1a5-4a09-bce9-f7972fb3e546","Revision":"#11","VariantName":"VECTOR-Surface_mounted_W310_H427_D151_12_Modular_Spacing-VE212L"} | 310 mm  [stored 1.01706 ft] | 427 mm  [stored 1.40092 ft] | 151 mm  [stored 0.495407 ft] | 2 | Yes | 12 | Yes | mit Ausschnitt | Yes | Yes | Yes | VE212L | 2 | 12 |
| VECTOR-Surface_mounted_W310_H427_D151_24_Modular_Spacing-VE212N | {"ObjectGuid":"03e6f95a-bdcf-4ad5-8e30-8306eb141510","ModelGuid":"49ec60d2-c561-4fc0-8b60-787ba45f202c","VariantGuid":"463241d1-9051-431d-8193-465042ba57ca","Revision":"#11","VariantName":"VECTOR-Surface_mounted_W310_H427_D151_24_Modular_Spacing-VE212N"} | 310 mm  [stored 1.01706 ft] | 427 mm  [stored 1.40092 ft] | 151 mm  [stored 0.495407 ft] | 2 | Yes | 24 | Yes | geschlossen | Yes | Yes | Yes | VE212N | 2 | 24 |
| VECTOR-Surface_mounted_W310_H427_D151_12_Modular_Spacing-VE212PN | {"ObjectGuid":"03e6f95a-bdcf-4ad5-8e30-8306eb141510","ModelGuid":"49ec60d2-c561-4fc0-8b60-787ba45f202c","VariantGuid":"ced611e9-4109-4197-8117-223dd0cf3f61","Revision":"#11","VariantName":"VECTOR-Surface_mounted_W310_H427_D151_12_Modular_Spacing-VE212PN"} | 310 mm  [stored 1.01706 ft] | 427 mm  [stored 1.40092 ft] | 151 mm  [stored 0.495407 ft] | 2 | Yes | 12 | Yes | geschlossen | No | No | Yes | VE212PN | 2 | 12 |
| VECTOR-Surface_mounted_W310_H427_D151_12_Modular_Spacing-VE212S | {"ObjectGuid":"03e6f95a-bdcf-4ad5-8e30-8306eb141510","ModelGuid":"49ec60d2-c561-4fc0-8b60-787ba45f202c","VariantGuid":"a4f9d9e2-82ab-4060-b9ca-197ddf63049e","Revision":"#11","VariantName":"VECTOR-Surface_mounted_W310_H427_D151_12_Modular_Spacing-VE212S"} | 310 mm  [stored 1.01706 ft] | 427 mm  [stored 1.40092 ft] | 151 mm  [stored 0.495407 ft] | 2 | Yes | 12 | No | geschlossen | Yes | Yes | Yes | VE212S | 2 | 12 |
| VECTOR-Surface_mounted_W310_H427_D151_12_Modular_Spacing-VE212SN | {"ObjectGuid":"03e6f95a-bdcf-4ad5-8e30-8306eb141510","ModelGuid":"49ec60d2-c561-4fc0-8b60-787ba45f202c","VariantGuid":"90dca5b2-7755-4063-91b3-8400c697aff5","Revision":"#11","VariantName":"VECTOR-Surface_mounted_W310_H427_D151_12_Modular_Spacing-VE212SN"} | 310 mm  [stored 1.01706 ft] | 427 mm  [stored 1.40092 ft] | 151 mm  [stored 0.495407 ft] | 2 | Yes | 12 | Yes | geschlossen | No | No | Yes | VE212SN | 2 | 12 |
| VECTOR-Surface_mounted_W418_H452_D151_18_Modular_Spacing-VE218AK | {"ObjectGuid":"03e6f95a-bdcf-4ad5-8e30-8306eb141510","ModelGuid":"49ec60d2-c561-4fc0-8b60-787ba45f202c","VariantGuid":"2289b807-37c6-4ce9-996c-1f3e60dd7ab1","Revision":"#11","VariantName":"VECTOR-Surface_mounted_W418_H452_D151_18_Modular_Spacing-VE218AK"} | 418 mm  [stored 1.37139 ft] | 452 mm  [stored 1.48294 ft] | 151 mm  [stored 0.495407 ft] | 2 | Yes | 18 | Yes | geschlossen | Yes | Yes | Yes | VE218AK | 2 | 18 |
| VECTOR-Surface_mounted_W418_H452_D151_36_Modular_Spacing-VE218DK | {"ObjectGuid":"03e6f95a-bdcf-4ad5-8e30-8306eb141510","ModelGuid":"49ec60d2-c561-4fc0-8b60-787ba45f202c","VariantGuid":"3bba2187-80fd-4537-b8ac-0784b8b5837d","Revision":"#11","VariantName":"VECTOR-Surface_mounted_W418_H452_D151_36_Modular_Spacing-VE218DK"} | 418 mm  [stored 1.37139 ft] | 452 mm  [stored 1.48294 ft] | 151 mm  [stored 0.495407 ft] | 2 | Yes | 36 | Yes | geschlossen | No | No | Yes | VE218DK | 2 | 36 |
| VECTOR-Surface_mounted_W418_H452_D151_18_Modular_Spacing-VE218DN | {"ObjectGuid":"03e6f95a-bdcf-4ad5-8e30-8306eb141510","ModelGuid":"49ec60d2-c561-4fc0-8b60-787ba45f202c","VariantGuid":"0875fca6-13a6-49b0-8691-1c375ba7f89e","Revision":"#11","VariantName":"VECTOR-Surface_mounted_W418_H452_D151_18_Modular_Spacing-VE218DN"} | 418 mm  [stored 1.37139 ft] | 452 mm  [stored 1.48294 ft] | 151 mm  [stored 0.495407 ft] | 2 | Yes | 18 | Yes | geschlossen | Yes | Yes | Yes | VE218DN | 2 | 18 |
| VECTOR-Surface_mounted_W418_H452_D151_18_Modular_Spacing-VE218F | {"ObjectGuid":"03e6f95a-bdcf-4ad5-8e30-8306eb141510","ModelGuid":"49ec60d2-c561-4fc0-8b60-787ba45f202c","VariantGuid":"40cefd4e-4eed-478c-99e9-6651af8c24fa","Revision":"#11","VariantName":"VECTOR-Surface_mounted_W418_H452_D151_18_Modular_Spacing-VE218F"} | 418 mm  [stored 1.37139 ft] | 452 mm  [stored 1.48294 ft] | 151 mm  [stored 0.495407 ft] | 2 | No | 18 | No | geschlossen | No | No | No | VE218F | 2 | 18 |
| VECTOR-Surface_mounted_W418_H452_D151_18_Modular_Spacing-VE218L | {"ObjectGuid":"03e6f95a-bdcf-4ad5-8e30-8306eb141510","ModelGuid":"49ec60d2-c561-4fc0-8b60-787ba45f202c","VariantGuid":"e03253d2-e9ce-4bbb-b0fa-c609af7765fb","Revision":"#11","VariantName":"VECTOR-Surface_mounted_W418_H452_D151_18_Modular_Spacing-VE218L"} | 418 mm  [stored 1.37139 ft] | 452 mm  [stored 1.48294 ft] | 151 mm  [stored 0.495407 ft] | 2 | Yes | 18 | Yes | mit Ausschnitt | Yes | Yes | Yes | VE218L | 2 | 18 |
| VECTOR-Surface_mounted_W418_H452_D151_36_Modular_Spacing-VE218N | {"ObjectGuid":"03e6f95a-bdcf-4ad5-8e30-8306eb141510","ModelGuid":"49ec60d2-c561-4fc0-8b60-787ba45f202c","VariantGuid":"b4acfa88-a8c3-4013-a6df-0be812a3ec4d","Revision":"#11","VariantName":"VECTOR-Surface_mounted_W418_H452_D151_36_Modular_Spacing-VE218N"} | 418 mm  [stored 1.37139 ft] | 452 mm  [stored 1.48294 ft] | 151 mm  [stored 0.495407 ft] | 2 | Yes | 36 | Yes | geschlossen | No | No | Yes | VE218N | 2 | 36 |
| VECTOR-Surface_mounted_W418_H452_D151_18_Modular_Spacing-VE218PN | {"ObjectGuid":"03e6f95a-bdcf-4ad5-8e30-8306eb141510","ModelGuid":"49ec60d2-c561-4fc0-8b60-787ba45f202c","VariantGuid":"d1e644d1-4220-4f40-88de-50d93dfd18d9","Revision":"#11","VariantName":"VECTOR-Surface_mounted_W418_H452_D151_18_Modular_Spacing-VE218PN"} | 418 mm  [stored 1.37139 ft] | 452 mm  [stored 1.48294 ft] | 151 mm  [stored 0.495407 ft] | 2 | Yes | 18 | Yes | geschlossen | No | No | Yes | VE218PN | 2 | 18 |
| VECTOR-Surface_mounted_W418_H452_D151_18_Modular_Spacing-VE218S | {"ObjectGuid":"03e6f95a-bdcf-4ad5-8e30-8306eb141510","ModelGuid":"49ec60d2-c561-4fc0-8b60-787ba45f202c","VariantGuid":"7864fc4b-5ae5-4e27-aff8-6636164325dd","Revision":"#11","VariantName":"VECTOR-Surface_mounted_W418_H452_D151_18_Modular_Spacing-VE218S"} | 418 mm  [stored 1.37139 ft] | 452 mm  [stored 1.48294 ft] | 151 mm  [stored 0.495407 ft] | 2 | Yes | 18 | No | geschlossen | Yes | Yes | Yes | VE218S | 2 | 18 |
| VECTOR-Surface_mounted_W418_H452_D151_18_Modular_Spacing-VE218SN | {"ObjectGuid":"03e6f95a-bdcf-4ad5-8e30-8306eb141510","ModelGuid":"49ec60d2-c561-4fc0-8b60-787ba45f202c","VariantGuid":"cd2daa1f-4eb8-434e-9e81-23fc99fae5d1","Revision":"#11","VariantName":"VECTOR-Surface_mounted_W418_H452_D151_18_Modular_Spacing-VE218SN"} | 418 mm  [stored 1.37139 ft] | 452 mm  [stored 1.48294 ft] | 151 mm  [stored 0.495407 ft] | 2 | Yes | 18 | Yes | mit Ausschnitt | No | No | Yes | VE218SN | 2 | 18 |
| VECTOR-Surface_mounted_W418_H602_D151_18_Modular_Spacing-VE318F | {"ObjectGuid":"03e6f95a-bdcf-4ad5-8e30-8306eb141510","ModelGuid":"49ec60d2-c561-4fc0-8b60-787ba45f202c","VariantGuid":"43378cf1-b6c0-4942-866d-fb963d6f364f","Revision":"#11","VariantName":"VECTOR-Surface_mounted_W418_H602_D151_18_Modular_Spacing-VE318F"} | 418 mm  [stored 1.37139 ft] | 602 mm  [stored 1.97507 ft] | 151 mm  [stored 0.495407 ft] | 3 | No | 18 | No | mit Ausschnitt | No | No | No | VE318F | 3 | 18 |
| VECTOR-Surface_mounted_W418_H602_D151_18_Modular_Spacing-VE318L | {"ObjectGuid":"03e6f95a-bdcf-4ad5-8e30-8306eb141510","ModelGuid":"49ec60d2-c561-4fc0-8b60-787ba45f202c","VariantGuid":"deccbbcd-6cdb-4c1a-8fe7-108926cdc028","Revision":"#11","VariantName":"VECTOR-Surface_mounted_W418_H602_D151_18_Modular_Spacing-VE318L"} | 418 mm  [stored 1.37139 ft] | 602 mm  [stored 1.97507 ft] | 151 mm  [stored 0.495407 ft] | 3 | Yes | 18 | Yes | mit Ausschnitt | Yes | Yes | Yes | VE318L | 3 | 18 |
| VECTOR-Surface_mounted_W418_H602_D151_54_Modular_Spacing-VE318N | {"ObjectGuid":"03e6f95a-bdcf-4ad5-8e30-8306eb141510","ModelGuid":"49ec60d2-c561-4fc0-8b60-787ba45f202c","VariantGuid":"f112cbb4-a923-47db-9236-8fa8ff00304c","Revision":"#11","VariantName":"VECTOR-Surface_mounted_W418_H602_D151_54_Modular_Spacing-VE318N"} | 418 mm  [stored 1.37139 ft] | 602 mm  [stored 1.97507 ft] | 151 mm  [stored 0.495407 ft] | 3 | Yes | 54 | Yes | geschlossen | Yes | Yes | Yes | VE318N | 3 | 54 |
| VECTOR-Surface_mounted_W418_H602_D151_18_Modular_Spacing-VE318PN | {"ObjectGuid":"03e6f95a-bdcf-4ad5-8e30-8306eb141510","ModelGuid":"49ec60d2-c561-4fc0-8b60-787ba45f202c","VariantGuid":"b25d7ddf-295f-4ac1-b43c-33bf122075df","Revision":"#11","VariantName":"VECTOR-Surface_mounted_W418_H602_D151_18_Modular_Spacing-VE318PN"} | 418 mm  [stored 1.37139 ft] | 602 mm  [stored 1.97507 ft] | 151 mm  [stored 0.495407 ft] | 3 | Yes | 18 | Yes | geschlossen | No | No | Yes | VE318PN | 3 | 18 |
| VECTOR-Surface_mounted_W418_H602_D151_18_Modular_Spacing-VE318S | {"ObjectGuid":"03e6f95a-bdcf-4ad5-8e30-8306eb141510","ModelGuid":"49ec60d2-c561-4fc0-8b60-787ba45f202c","VariantGuid":"10d15475-3d01-4d58-a49a-3a9322acb4d0","Revision":"#11","VariantName":"VECTOR-Surface_mounted_W418_H602_D151_18_Modular_Spacing-VE318S"} | 418 mm  [stored 1.37139 ft] | 602 mm  [stored 1.97507 ft] | 151 mm  [stored 0.495407 ft] | 3 | Yes | 18 | No | geschlossen | Yes | Yes | Yes | VE318S | 3 | 18 |
| VECTOR-Surface_mounted_W418_H602_D151_18_Modular_Spacing-VE318SN | {"ObjectGuid":"03e6f95a-bdcf-4ad5-8e30-8306eb141510","ModelGuid":"49ec60d2-c561-4fc0-8b60-787ba45f202c","VariantGuid":"ec47373e-763f-41e3-b4dd-b6f6a8ad6ab3","Revision":"#11","VariantName":"VECTOR-Surface_mounted_W418_H602_D151_18_Modular_Spacing-VE318SN"} | 418 mm  [stored 1.37139 ft] | 602 mm  [stored 1.97507 ft] | 151 mm  [stored 0.495407 ft] | 3 | Yes | 18 | Yes | mit Ausschnitt | No | No | Yes | VE318SN | 3 | 18 |
| VECTOR-Surface_mounted_W310_H677_D151_12_Modular_Spacing-VE412AK | {"ObjectGuid":"03e6f95a-bdcf-4ad5-8e30-8306eb141510","ModelGuid":"49ec60d2-c561-4fc0-8b60-787ba45f202c","VariantGuid":"ea8114db-3225-4f07-b339-5c9b5b53128b","Revision":"#11","VariantName":"VECTOR-Surface_mounted_W310_H677_D151_12_Modular_Spacing-VE412AK"} | 310 mm  [stored 1.01706 ft] | 677 mm  [stored 2.22113 ft] | 151 mm  [stored 0.495407 ft] | 4 | Yes | 12 | Yes | geschlossen | Yes | Yes | Yes | VE412AK | 4 | 12 |
| VECTOR-Surface_mounted_W310_H677_D151_48_Modular_Spacing-VE412DK | {"ObjectGuid":"03e6f95a-bdcf-4ad5-8e30-8306eb141510","ModelGuid":"49ec60d2-c561-4fc0-8b60-787ba45f202c","VariantGuid":"38f0733a-528a-4156-9850-e8bdf2174f5e","Revision":"#11","VariantName":"VECTOR-Surface_mounted_W310_H677_D151_48_Modular_Spacing-VE412DK"} | 310 mm  [stored 1.01706 ft] | 677 mm  [stored 2.22113 ft] | 151 mm  [stored 0.495407 ft] | 4 | Yes | 48 | Yes | geschlossen | No | No | Yes | VE412DK | 4 | 48 |
| VECTOR-Surface_mounted_W310_H677_D151_12_Modular_Spacing-VE412DN | {"ObjectGuid":"03e6f95a-bdcf-4ad5-8e30-8306eb141510","ModelGuid":"49ec60d2-c561-4fc0-8b60-787ba45f202c","VariantGuid":"fb12cbe8-73cd-4691-b32e-93c088428df1","Revision":"#11","VariantName":"VECTOR-Surface_mounted_W310_H677_D151_12_Modular_Spacing-VE412DN"} | 310 mm  [stored 1.01706 ft] | 677 mm  [stored 2.22113 ft] | 151 mm  [stored 0.495407 ft] | 4 | Yes | 12 | Yes | geschlossen | Yes | Yes | Yes | VE412DN | 4 | 12 |
| VECTOR-Surface_mounted_W310_H677_D151_12_Modular_Spacing-VE412F | {"ObjectGuid":"03e6f95a-bdcf-4ad5-8e30-8306eb141510","ModelGuid":"49ec60d2-c561-4fc0-8b60-787ba45f202c","VariantGuid":"82c5b276-3320-4a5e-9da3-442ff85b5107","Revision":"#11","VariantName":"VECTOR-Surface_mounted_W310_H677_D151_12_Modular_Spacing-VE412F"} | 310 mm  [stored 1.01706 ft] | 677 mm  [stored 2.22113 ft] | 151 mm  [stored 0.495407 ft] | 4 | No | 12 | No | geschlossen | No | No | No | VE412F | 4 | 12 |
| VECTOR-Surface_mounted_W310_H677_D151_12_Modular_Spacing-VE412L | {"ObjectGuid":"03e6f95a-bdcf-4ad5-8e30-8306eb141510","ModelGuid":"49ec60d2-c561-4fc0-8b60-787ba45f202c","VariantGuid":"0016aad4-3d4d-446b-b7cc-fe855d116879","Revision":"#11","VariantName":"VECTOR-Surface_mounted_W310_H677_D151_12_Modular_Spacing-VE412L"} | 310 mm  [stored 1.01706 ft] | 677 mm  [stored 2.22113 ft] | 151 mm  [stored 0.495407 ft] | 4 | Yes | 12 | Yes | mit Ausschnitt | Yes | Yes | Yes | VE412L | 4 | 12 |
| VECTOR-Surface_mounted_W310_H677_D151_48_Modular_Spacing-VE412N | {"ObjectGuid":"03e6f95a-bdcf-4ad5-8e30-8306eb141510","ModelGuid":"49ec60d2-c561-4fc0-8b60-787ba45f202c","VariantGuid":"2a233efe-fdd6-409b-83b5-b58c56740499","Revision":"#11","VariantName":"VECTOR-Surface_mounted_W310_H677_D151_48_Modular_Spacing-VE412N"} | 310 mm  [stored 1.01706 ft] | 677 mm  [stored 2.22113 ft] | 151 mm  [stored 0.495407 ft] | 4 | Yes | 48 | Yes | geschlossen | No | No | Yes | VE412N | 4 | 48 |
| VECTOR-Surface_mounted_W310_H677_D151_12_Modular_Spacing-VE412PN | {"ObjectGuid":"03e6f95a-bdcf-4ad5-8e30-8306eb141510","ModelGuid":"49ec60d2-c561-4fc0-8b60-787ba45f202c","VariantGuid":"c2aaa507-8f22-4a3d-b207-203d3da28564","Revision":"#11","VariantName":"VECTOR-Surface_mounted_W310_H677_D151_12_Modular_Spacing-VE412PN"} | 310 mm  [stored 1.01706 ft] | 677 mm  [stored 2.22113 ft] | 151 mm  [stored 0.495407 ft] | 4 | Yes | 12 | Yes | geschlossen | No | No | Yes | VE412PN | 4 | 12 |
| VECTOR-Surface_mounted_W310_H677_D151_12_Modular_Spacing-VE412S | {"ObjectGuid":"03e6f95a-bdcf-4ad5-8e30-8306eb141510","ModelGuid":"49ec60d2-c561-4fc0-8b60-787ba45f202c","VariantGuid":"2060f6d1-d0db-4e67-afb0-facf9fa38084","Revision":"#11","VariantName":"VECTOR-Surface_mounted_W310_H677_D151_12_Modular_Spacing-VE412S"} | 310 mm  [stored 1.01706 ft] | 677 mm  [stored 2.22113 ft] | 151 mm  [stored 0.495407 ft] | 4 | Yes | 12 | No | geschlossen | Yes | Yes | Yes | VE412S | 4 | 12 |
| VECTOR-Surface_mounted_W310_H677_D151_12_Modular_Spacing-VE412SN | {"ObjectGuid":"03e6f95a-bdcf-4ad5-8e30-8306eb141510","ModelGuid":"49ec60d2-c561-4fc0-8b60-787ba45f202c","VariantGuid":"e74cd546-5514-4689-b48d-d1409375e047","Revision":"#11","VariantName":"VECTOR-Surface_mounted_W310_H677_D151_12_Modular_Spacing-VE412SN"} | 310 mm  [stored 1.01706 ft] | 677 mm  [stored 2.22113 ft] | 151 mm  [stored 0.495407 ft] | 4 | Yes | 12 | Yes | mit Ausschnitt | No | No | Yes | VE412SN | 4 | 12 |

note: [stored X ft] marks values corroborated as IEEE doubles in the binary element streams (Revit-internal decimal feet)

## geometry (parser evidence)
native form markers: Sweep x13
no freeform markers — native parametric forms only
